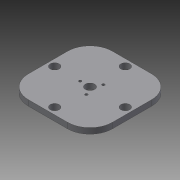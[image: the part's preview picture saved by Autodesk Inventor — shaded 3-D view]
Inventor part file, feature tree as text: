
AUTODESK INVENTOR PART (.ipt)
format: ipt  version: 2015 (Build 190159000, 159)  size: 117,248 bytes
history: native  units: in
note: dims shown in document units (in); Inventor stores cm internally (conversion verified against a paired STEP export)
features: extrude x1, fillet x1, sketch x1
ambient origin geometry x8: Origin, YZ Plane, XZ Plane, XY Plane, X Axis, Y Axis, Z Axis, Center Point
bodies: Body1 (feature_tree)
feature tree (3):
  extrude  "Extrusion6"  TaperAngle=120.0deg  [1 undecoded]
  fillet  "Fillet1"  Radius=0.4375in
  sketch  "Sketch3"  dims[d19=120.0deg d20=120.0deg d21=0.4375in d22=0.4375in d23=0.4375in d24=0.1174in d25=0.1174in d26=0.1174in d27=3.1496in d28=3.1496in d29=0.3976in d30=0.3976in d31=3.75in d32=3.75in d33=0.25in d34=0.0in d35=1.0in d36=0.4134in]
note: 1 required parameter value undecoded (feature->parameter linkage not recoverable at this tier; creation-order binding heuristic only, values carry confidence <= 0.55)
